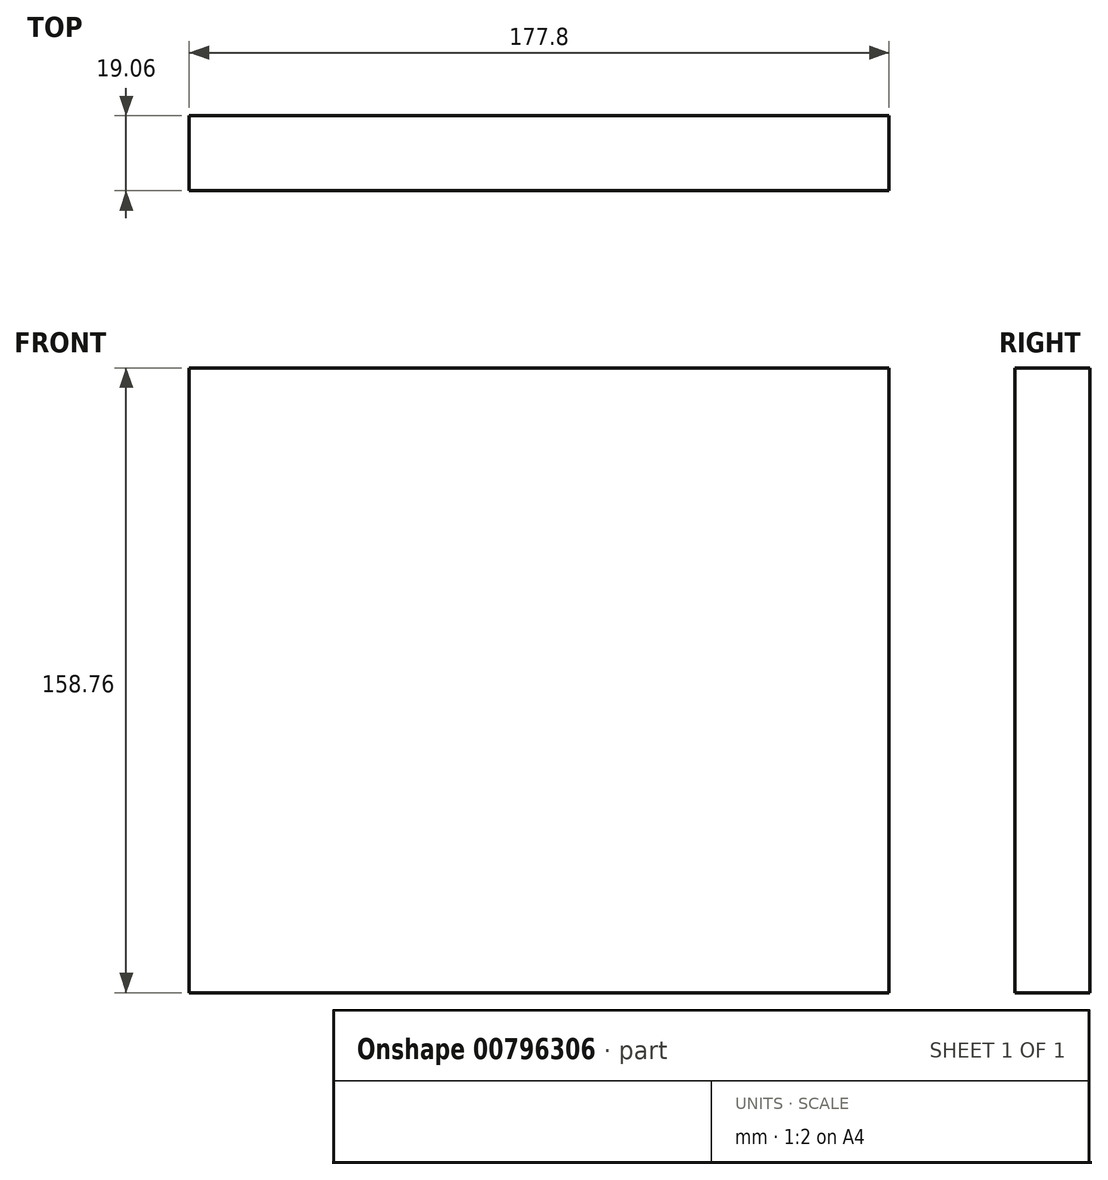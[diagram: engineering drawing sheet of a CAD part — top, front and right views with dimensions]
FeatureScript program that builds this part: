
annotation { "Feature Type Name" : "Feature", "Feature Type Description" : "" }
export const myFeature = defineFeature(function(context is Context, id is Id, definition is map)
    precondition{}
    {
        {
            var Q0;
            Q0=qCreatedBy(makeId("Front.planeOp"),FACE);
            var sketch = newSketch(context, id + "F0", { "sketchPlane" : qUnion([Q0])});
            skLineSegment(sketch, "E0.bottom", {"start": v(-88.9, 79.38) * mm, "end": v(88.9, 79.38) * mm});
            skLineSegment(sketch, "E0.top", {"start": v(-88.9, -79.38) * mm, "end": v(88.9, -79.38) * mm});
            skLineSegment(sketch, "E0.left", {"start": v(-88.9, 79.38) * mm, "end": v(-88.9, -79.38) * mm});
            skLineSegment(sketch, "E0.right", {"start": v(88.9, 79.38) * mm, "end": v(88.9, -79.38) * mm});
            skPoint(sketch, "E0.middle", {"position": v(0, 0) * mm});
            skSolve(sketch);
        }
        {
            var Q0;
            Q0=makeQuery(id+"F0.imprint","IMPRINT",FACE,{"disambiguationData":[TD([[makeQuery(id+"F0.imprint","IMPRINT",EDGE,{"derivedFrom":sQuery(id+"F0.wireOp",EDGE,"E0.bottom")}),-1.0]])]});
            extrude(context, id + "F1", {"entities" : qUnion([Q0]), "endBound" : BoundingType.SYMMETRIC, "depth" : 19.05 * mm, "offsetDistance" : 25.4 * mm});
        }
    });
